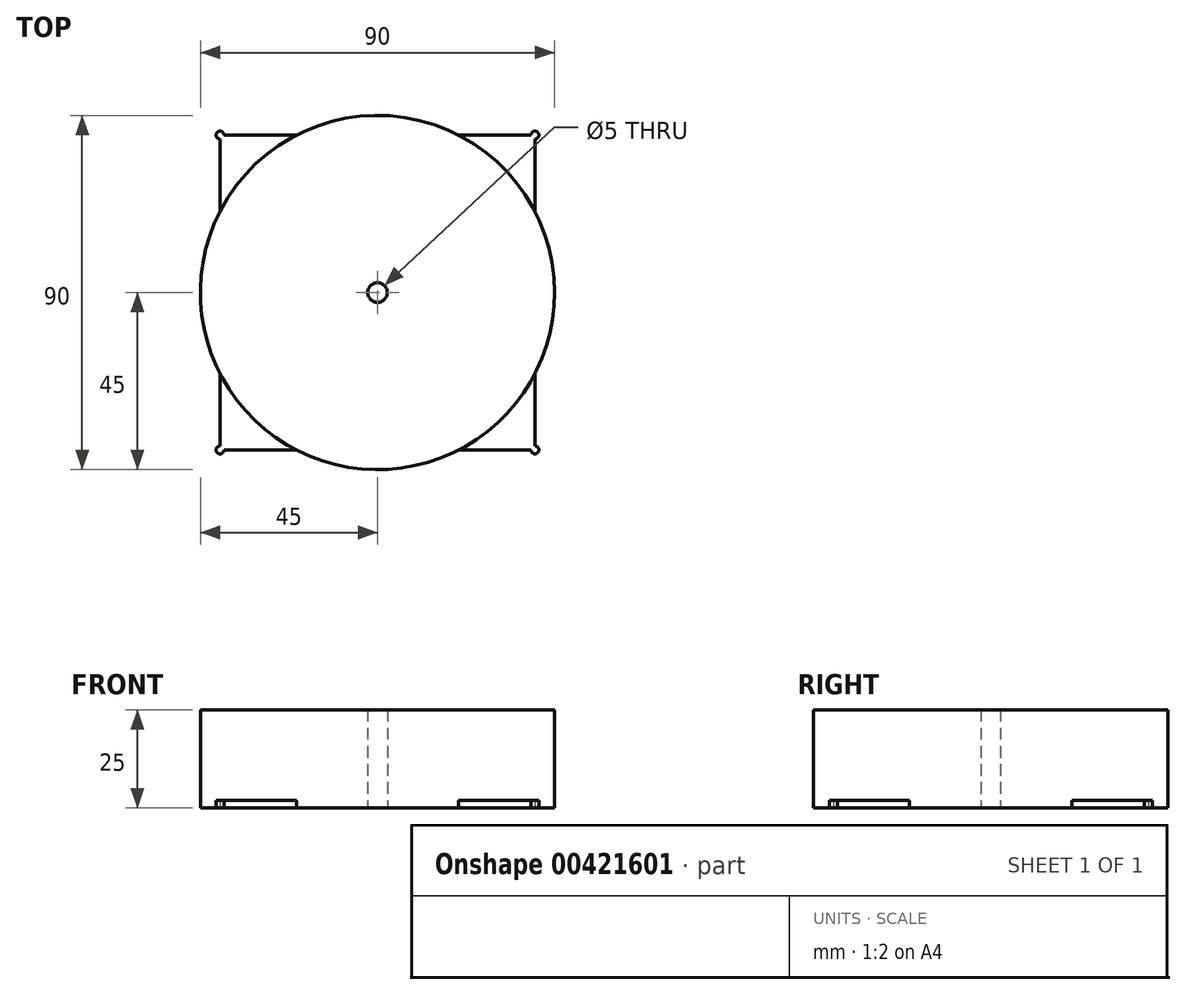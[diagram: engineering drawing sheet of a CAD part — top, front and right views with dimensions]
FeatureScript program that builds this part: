
annotation { "Feature Type Name" : "Feature", "Feature Type Description" : "" }
export const myFeature = defineFeature(function(context is Context, id is Id, definition is map)
    precondition{}
    {
        {
            var Q0;
            Q0=qCreatedBy(makeId("Top.planeOp"),FACE);
            var sketch = newSketch(context, id + "F0", { "sketchPlane" : qUnion([Q0])});
            skPoint(sketch, "E0.middle", {"position": v(0, 0) * mm});
            skCircle(sketch, "E1", {"center": v(40, 40) * mm, "radius": 1 * mm});
            skCircle(sketch, "E2", {"center": v(40, -40) * mm, "radius": 1 * mm});
            skCircle(sketch, "E3", {"center": v(-40, -40) * mm, "radius": 1 * mm});
            skCircle(sketch, "E4", {"center": v(-40, 40) * mm, "radius": 1 * mm});
            skCircle(sketch, "E5", {"center": v(0, 0) * mm, "radius": 45 * mm});
            skCircle(sketch, "E6", {"center": v(0, 0) * mm, "radius": 2.5 * mm});
            skLineSegment(sketch, "E7", {"start": v(-40, -40) * mm, "end": v(-20.62, -40) * mm});
            skLineSegment(sketch, "E8", {"start": v(40, -40) * mm, "end": v(20.62, -40) * mm});
            skLineSegment(sketch, "E9", {"start": v(-40, -40) * mm, "end": v(-40, -20.62) * mm});
            skLineSegment(sketch, "E10", {"start": v(40, -40) * mm, "end": v(40, -20.62) * mm});
            skLineSegment(sketch, "E11", {"start": v(-40, 40) * mm, "end": v(-40, 20.62) * mm});
            skLineSegment(sketch, "E12", {"start": v(-40, 40) * mm, "end": v(-20.62, 40) * mm});
            skLineSegment(sketch, "E13", {"start": v(40, 40) * mm, "end": v(20.62, 40) * mm});
            skLineSegment(sketch, "E14", {"start": v(40, 40) * mm, "end": v(40, 20.62) * mm});
            skSolve(sketch);
        }
        {
            var Q0;
            Q0=makeQuery(id+"F0.imprint","IMPRINT",FACE,{"disambiguationData":[TD([[makeQuery(id+"F0.imprint","IMPRINT",EDGE,{"derivedFrom":sQuery(id+"F0.wireOp",EDGE,"E5")}),-1.0]])]});
            var Q1;
            Q1=makeQuery(id+"F0.imprint","IMPRINT",FACE,{"disambiguationData":[TD([[makeQuery(id+"F0.imprint","IMPRINT",EDGE,{"derivedFrom":sQuery(id+"F0.wireOp",EDGE,"E5")}),1.0]])]});
            var Q2;
            {var subQ0=sQuery(id+"F0.wireOp",EDGE,"E0.right");var subQ1=sQuery(id+"F0.wireOp",EDGE,"E0.bottom");var subQ2=makeQuery(id+"F0.imprint","INTERSECT",VERTEX,{"derivedFrom":[subQ1,subQ0]});Q2=makeQuery(id+"F0.imprint","IMPRINT",FACE,{"disambiguationData":[TD([[makeQuery(id+"F0.imprint","IMPRINT",EDGE,{"disambiguationData":[TD([[subQ2,1.0]])],"derivedFrom":subQ1}),-1.0]])]});}
            var Q3;
            {var subQ0=sQuery(id+"F0.wireOp",EDGE,"E0.right");var subQ1=sQuery(id+"F0.wireOp",EDGE,"E0.bottom");var subQ2=makeQuery(id+"F0.imprint","INTERSECT",VERTEX,{"derivedFrom":[subQ1,subQ0]});Q3=makeQuery(id+"F0.imprint","IMPRINT",FACE,{"disambiguationData":[TD([[makeQuery(id+"F0.imprint","IMPRINT",EDGE,{"disambiguationData":[TD([[subQ2,1.0]])],"derivedFrom":subQ1}),1.0]])]});}
            var Q4;
            {var subQ0=sQuery(id+"F0.wireOp",EDGE,"E0.left");var subQ1=sQuery(id+"F0.wireOp",EDGE,"E0.bottom");var subQ2=makeQuery(id+"F0.imprint","INTERSECT",VERTEX,{"derivedFrom":[subQ1,subQ0]});Q4=makeQuery(id+"F0.imprint","IMPRINT",FACE,{"disambiguationData":[TD([[makeQuery(id+"F0.imprint","IMPRINT",EDGE,{"disambiguationData":[TD([[subQ2,-1.0]])],"derivedFrom":subQ1}),1.0]])]});}
            var Q5;
            {var subQ0=sQuery(id+"F0.wireOp",EDGE,"E0.left");var subQ1=sQuery(id+"F0.wireOp",EDGE,"E0.bottom");var subQ2=makeQuery(id+"F0.imprint","INTERSECT",VERTEX,{"derivedFrom":[subQ1,subQ0]});Q5=makeQuery(id+"F0.imprint","IMPRINT",FACE,{"disambiguationData":[TD([[makeQuery(id+"F0.imprint","IMPRINT",EDGE,{"disambiguationData":[TD([[subQ2,-1.0]])],"derivedFrom":subQ1}),-1.0]])]});}
            var Q6;
            {var subQ0=sQuery(id+"F0.wireOp",EDGE,"E0.left");var subQ1=sQuery(id+"F0.wireOp",EDGE,"E0.top");var subQ2=makeQuery(id+"F0.imprint","INTERSECT",VERTEX,{"derivedFrom":[subQ1,subQ0]});Q6=makeQuery(id+"F0.imprint","IMPRINT",FACE,{"disambiguationData":[TD([[makeQuery(id+"F0.imprint","IMPRINT",EDGE,{"disambiguationData":[TD([[subQ2,-1.0]])],"derivedFrom":subQ1}),1.0]])]});}
            var Q7;
            {var subQ0=sQuery(id+"F0.wireOp",EDGE,"E0.left");var subQ1=sQuery(id+"F0.wireOp",EDGE,"E0.top");var subQ2=makeQuery(id+"F0.imprint","INTERSECT",VERTEX,{"derivedFrom":[subQ1,subQ0]});Q7=makeQuery(id+"F0.imprint","IMPRINT",FACE,{"disambiguationData":[TD([[makeQuery(id+"F0.imprint","IMPRINT",EDGE,{"disambiguationData":[TD([[subQ2,-1.0]])],"derivedFrom":subQ1}),-1.0]])]});}
            var Q8;
            {var subQ0=sQuery(id+"F0.wireOp",EDGE,"E0.right");var subQ1=sQuery(id+"F0.wireOp",EDGE,"E0.top");var subQ2=makeQuery(id+"F0.imprint","INTERSECT",VERTEX,{"derivedFrom":[subQ1,subQ0]});Q8=makeQuery(id+"F0.imprint","IMPRINT",FACE,{"disambiguationData":[TD([[makeQuery(id+"F0.imprint","IMPRINT",EDGE,{"disambiguationData":[TD([[subQ2,1.0]])],"derivedFrom":subQ1}),1.0]])]});}
            var Q9;
            {var subQ0=sQuery(id+"F0.wireOp",EDGE,"E0.right");var subQ1=sQuery(id+"F0.wireOp",EDGE,"E0.top");var subQ2=makeQuery(id+"F0.imprint","INTERSECT",VERTEX,{"derivedFrom":[subQ1,subQ0]});Q9=makeQuery(id+"F0.imprint","IMPRINT",FACE,{"disambiguationData":[TD([[makeQuery(id+"F0.imprint","IMPRINT",EDGE,{"disambiguationData":[TD([[subQ2,1.0]])],"derivedFrom":subQ1}),-1.0]])]});}
            var Q10;
            {var subQ0=sQuery(id+"F0.wireOp",EDGE,"E11");var subQ1=sQuery(id+"F0.wireOp",EDGE,"E4");var subQ2=makeQuery(id+"F0.imprint","INTERSECT",VERTEX,{"derivedFrom":[subQ1,subQ0]});Q10=makeQuery(id+"F0.imprint","IMPRINT",FACE,{"disambiguationData":[TD([[makeQuery(id+"F0.imprint","IMPRINT",EDGE,{"disambiguationData":[TD([[subQ2,1.0]])],"derivedFrom":subQ1}),1.0]])]});}
            var Q11;
            {var subQ0=sQuery(id+"F0.wireOp",EDGE,"E11");var subQ1=sQuery(id+"F0.wireOp",EDGE,"E4");var subQ2=makeQuery(id+"F0.imprint","INTERSECT",VERTEX,{"derivedFrom":[subQ1,subQ0]});Q11=makeQuery(id+"F0.imprint","IMPRINT",FACE,{"disambiguationData":[TD([[makeQuery(id+"F0.imprint","IMPRINT",EDGE,{"disambiguationData":[TD([[subQ2,-1.0]])],"derivedFrom":subQ1}),1.0]])]});}
            var Q12;
            {var subQ0=sQuery(id+"F0.wireOp",EDGE,"E13");var subQ1=sQuery(id+"F0.wireOp",EDGE,"E1");var subQ2=makeQuery(id+"F0.imprint","INTERSECT",VERTEX,{"derivedFrom":[subQ1,subQ0]});Q12=makeQuery(id+"F0.imprint","IMPRINT",FACE,{"disambiguationData":[TD([[makeQuery(id+"F0.imprint","IMPRINT",EDGE,{"disambiguationData":[TD([[subQ2,-1.0]])],"derivedFrom":subQ1}),1.0]])]});}
            var Q13;
            {var subQ0=sQuery(id+"F0.wireOp",EDGE,"E13");var subQ1=sQuery(id+"F0.wireOp",EDGE,"E1");var subQ2=makeQuery(id+"F0.imprint","INTERSECT",VERTEX,{"derivedFrom":[subQ1,subQ0]});Q13=makeQuery(id+"F0.imprint","IMPRINT",FACE,{"disambiguationData":[TD([[makeQuery(id+"F0.imprint","IMPRINT",EDGE,{"disambiguationData":[TD([[subQ2,1.0]])],"derivedFrom":subQ1}),1.0]])]});}
            var Q14;
            {var subQ0=sQuery(id+"F0.wireOp",EDGE,"E8");var subQ1=sQuery(id+"F0.wireOp",EDGE,"E2");var subQ2=makeQuery(id+"F0.imprint","INTERSECT",VERTEX,{"derivedFrom":[subQ1,subQ0]});Q14=makeQuery(id+"F0.imprint","IMPRINT",FACE,{"disambiguationData":[TD([[makeQuery(id+"F0.imprint","IMPRINT",EDGE,{"disambiguationData":[TD([[subQ2,-1.0]])],"derivedFrom":subQ1}),1.0]])]});}
            var Q15;
            {var subQ0=sQuery(id+"F0.wireOp",EDGE,"E8");var subQ1=sQuery(id+"F0.wireOp",EDGE,"E2");var subQ2=makeQuery(id+"F0.imprint","INTERSECT",VERTEX,{"derivedFrom":[subQ1,subQ0]});Q15=makeQuery(id+"F0.imprint","IMPRINT",FACE,{"disambiguationData":[TD([[makeQuery(id+"F0.imprint","IMPRINT",EDGE,{"disambiguationData":[TD([[subQ2,1.0]])],"derivedFrom":subQ1}),1.0]])]});}
            var Q16;
            {var subQ0=sQuery(id+"F0.wireOp",EDGE,"E7");var subQ1=sQuery(id+"F0.wireOp",EDGE,"E3");var subQ2=makeQuery(id+"F0.imprint","INTERSECT",VERTEX,{"derivedFrom":[subQ1,subQ0]});Q16=makeQuery(id+"F0.imprint","IMPRINT",FACE,{"disambiguationData":[TD([[makeQuery(id+"F0.imprint","IMPRINT",EDGE,{"disambiguationData":[TD([[subQ2,1.0]])],"derivedFrom":subQ1}),1.0]])]});}
            var Q17;
            {var subQ0=sQuery(id+"F0.wireOp",EDGE,"E7");var subQ1=sQuery(id+"F0.wireOp",EDGE,"E3");var subQ2=makeQuery(id+"F0.imprint","INTERSECT",VERTEX,{"derivedFrom":[subQ1,subQ0]});Q17=makeQuery(id+"F0.imprint","IMPRINT",FACE,{"disambiguationData":[TD([[makeQuery(id+"F0.imprint","IMPRINT",EDGE,{"disambiguationData":[TD([[subQ2,-1.0]])],"derivedFrom":subQ1}),1.0]])]});}
            extrude(context, id + "F1", {"entities" : qUnion([Q0, Q1, Q2, Q3, Q4, Q5, Q6, Q7, Q8, Q9, Q10, Q11, Q12, Q13, Q14, Q15, Q16, Q17]), "depth" : 2 * mm});
        }
        {
            var Q0;
            Q0=makeQuery(id+"F0.imprint","IMPRINT",FACE,{"disambiguationData":[TD([[makeQuery(id+"F0.imprint","IMPRINT",EDGE,{"derivedFrom":sQuery(id+"F0.wireOp",EDGE,"E5")}),1.0]])]});
            extrude(context, id + "F2", {"entities" : qUnion([Q0]), "operationType" : NewBodyOperationType.ADD, "depth" : 25 * mm});
        }
    });
